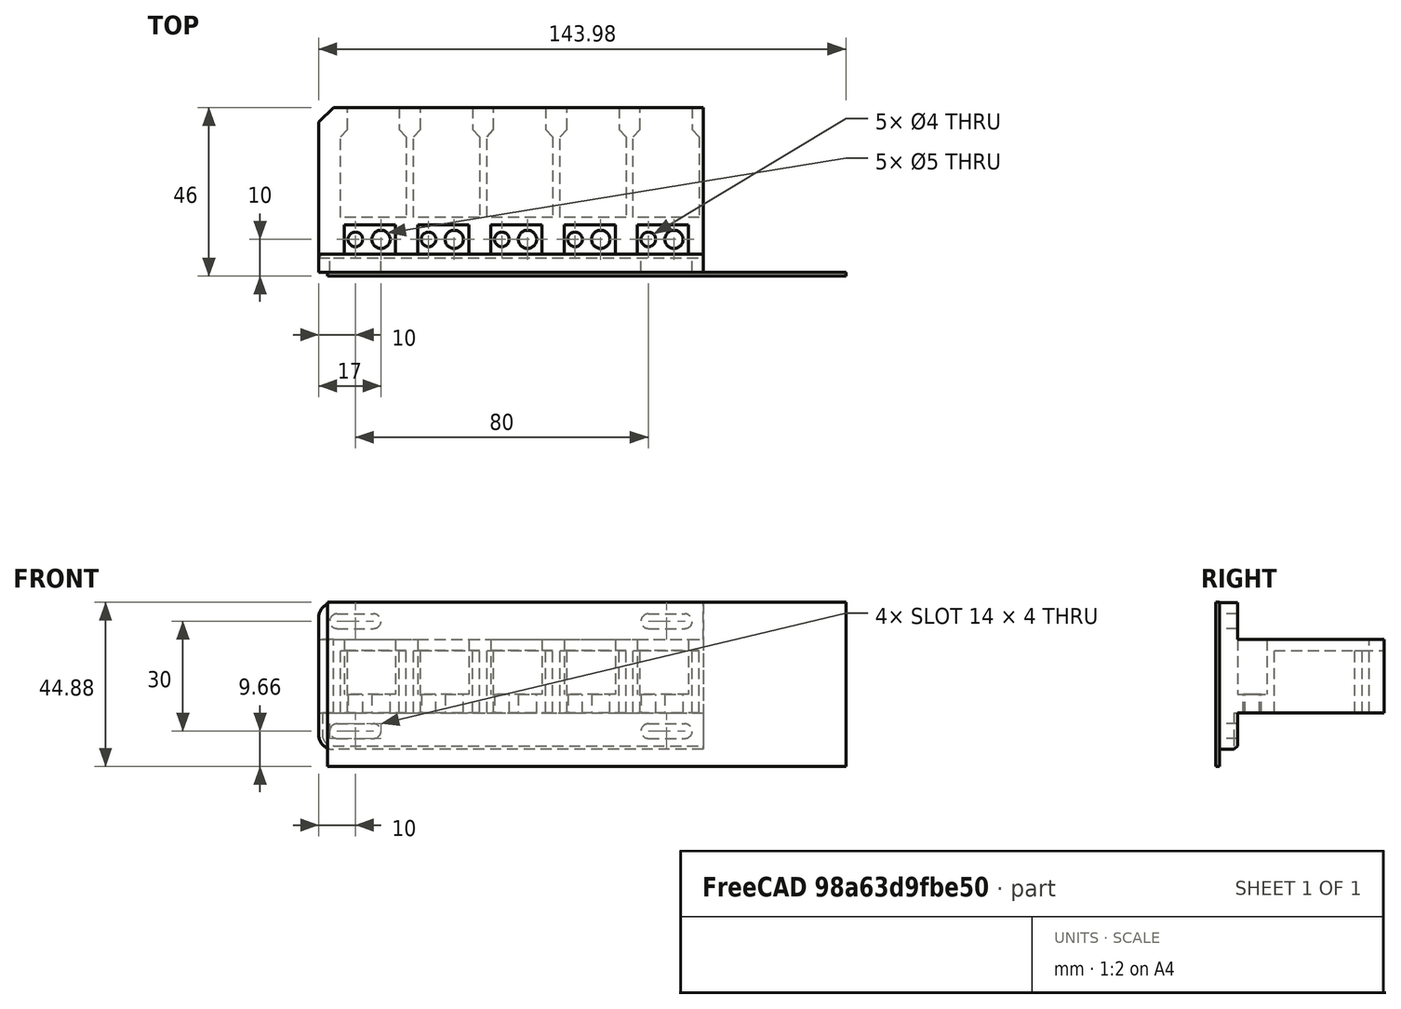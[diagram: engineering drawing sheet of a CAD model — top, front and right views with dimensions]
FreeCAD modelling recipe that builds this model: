
FCSTD DOCUMENT  (FreeCAD 0.18.4R)
Label: switchholder
License: All rights reserved
LicenseURL: http://en.wikipedia.org/wiki/All_rights_reserved
objects: Sketcher::SketchObject×7, Mesh::Feature×5, PartDesign::Pocket×5, PartDesign::LinearPattern×3, PartDesign::Pad×2, PartDesign::Body×2, PartDesign::Chamfer×2, PartDesign::Fillet×1
note: 29 computed .brp shape members not serialized (recipe doc carries the construction recipe); baked Part::Feature solids carry a one-line shape summary decoded from their .brp

FEATURE [Mesh::Feature] v10
  Placement = pos=(0,38,0) rot=(0,0,1;0rad)
FEATURE [Mesh::Feature] v011
  Placement = pos=(20,38,0) rot=(0,0,1;0rad)
FEATURE [Mesh::Feature] v012
  Placement = pos=(-20,38,0) rot=(0,0,1;0rad)
FEATURE [Sketcher::SketchObject] Sketch
  MapMode = 5
  Placement = pos=(0,0,0) rot=(1,0,0;1.5708rad)
  Support = -> [XZ_Plane001]
  sketch-geometry (4):
    g0: LineSegment StartX=-52.6197 StartY=20.2239 StartZ=0 EndX=88.9826 EndY=20.2239 EndZ=0
    g1: LineSegment StartX=88.9826 StartY=20.2239 StartZ=0 EndX=88.9826 EndY=-24.6555 EndZ=0
    g2: LineSegment StartX=88.9826 StartY=-24.6555 StartZ=0 EndX=-52.6197 EndY=-24.6555 EndZ=0
    g3: LineSegment StartX=-52.6197 StartY=-24.6555 StartZ=0 EndX=-52.6197 EndY=20.2239 EndZ=0
  constraints (8):
    c: Coincident(g0,g1)
    c: Coincident(g1,g2)
    c: Coincident(g2,g3)
    c: Coincident(g3,g0)
    c: Horizontal(g0)
    c: Horizontal(g2)
    c: Vertical(g1)
    c: Vertical(g3)
FEATURE [PartDesign::Pad] Pad
  Length = 1
  Length2 = 100
  Placement = pos=(0,0,0) rot=(1,0,0;1.5708rad)
  Profile = -> Sketch
  Refine = true
  Type = 0
FEATURE [PartDesign::Body] Body001
  Group = -> [Sketch,Pad]
  Origin = -> Origin001
  Tip = -> Pad
FEATURE [Mesh::Feature] v013
  Placement = pos=(-40,38,0) rot=(0,0,1;0rad)
FEATURE [Mesh::Feature] v014
  Placement = pos=(40,38,0) rot=(0,0,1;0rad)
FEATURE [Sketcher::SketchObject] Sketch001
  MapMode = 5
  Placement = pos=(0,0,0) rot=(1,0,0;1.5708rad)
  Support = -> [XZ_Plane]
  sketch-geometry (4):
    g0: LineSegment StartX=-55 StartY=20 StartZ=0 EndX=50 EndY=20 EndZ=0
    g1: LineSegment StartX=50 StartY=20 StartZ=0 EndX=50 EndY=-20 EndZ=0
    g2: LineSegment StartX=50 StartY=-20 StartZ=0 EndX=-55 EndY=-20 EndZ=0
    g3: LineSegment StartX=-55 StartY=-20 StartZ=0 EndX=-55 EndY=20 EndZ=0
  constraints (11):
    c: Coincident(g0,g1)
    c: Coincident(g1,g2)
    c: Coincident(g2,g3)
    c: Coincident(g3,g0)
    c: Horizontal(g2)
    c: Vertical(g1)
    c: Vertical(g3)
    c: DistanceX(g0,g0) = 105
    c: DistanceY(g3,g3) = 40
    c: DistanceY(g-1,g0) = 20
    c: DistanceX(g-1,g0) = 50
FEATURE [PartDesign::Pad] Pad001
  Length = 45
  Length2 = 100
  Placement = pos=(0,0,0) rot=(1,0,0;1.5708rad)
  Profile = -> Sketch001
  Refine = true
  Reversed = true
  Type = 0
FEATURE [Sketcher::SketchObject] Sketch002
  ExternalGeometry = -> [Pad001]
  MapMode = 5
  Placement = pos=(-55,0,0) rot=(0.707107,0,-0.707107;3.14159rad)
  Support = -> [Pad001]
  sketch-geometry (8):
    g0: LineSegment StartX=-20 StartY=-45 StartZ=0 EndX=-10 EndY=-45 EndZ=0
    g1: LineSegment StartX=-10 StartY=-45 StartZ=0 EndX=-10 EndY=-5 EndZ=0
    g2: LineSegment StartX=-10 StartY=-5 StartZ=0 EndX=-20 EndY=-5 EndZ=0
    g3: LineSegment StartX=-20 StartY=-5 StartZ=0 EndX=-20 EndY=-45 EndZ=0
    g4: LineSegment StartX=20 StartY=-45 StartZ=0 EndX=10 EndY=-45 EndZ=0
    g5: LineSegment StartX=10 StartY=-45 StartZ=0 EndX=10 EndY=-5 EndZ=0
    g6: LineSegment StartX=10 StartY=-5 StartZ=0 EndX=20 EndY=-5 EndZ=0
    g7: LineSegment StartX=20 StartY=-5 StartZ=0 EndX=20 EndY=-45 EndZ=0
  constraints (22):
    c: Coincident(g0,g1)
    c: Coincident(g1,g2)
    c: Coincident(g2,g3)
    c: Coincident(g3,g0)
    c: Horizontal(g0)
    c: Horizontal(g2)
    c: Vertical(g1)
    c: Vertical(g3)
    c: Coincident(g0,g-3)
    c: Coincident(g4,g5)
    c: Coincident(g5,g6)
    c: Coincident(g6,g7)
    c: Coincident(g7,g4)
    c: Horizontal(g4)
    c: Horizontal(g6)
    c: Vertical(g5)
    c: Vertical(g7)
    c: Coincident(g4,g-4)
    c: Equal(g4,g0)
    c: Horizontal(g1,g5)
    c: DistanceY(g2,g-3) = 5
    c: DistanceX(g2,g2) = 10
FEATURE [PartDesign::Pocket] Pocket
  BaseFeature = -> Pad001
  Length = 5
  Length2 = 100
  Placement = pos=(0,0,0) rot=(1,0,0;1.5708rad)
  Profile = -> Sketch002
  Refine = true
  Type = 1
FEATURE [Sketcher::SketchObject] Sketch003
  ExternalGeometry = -> [Pocket]
  MapMode = 5
  Placement = pos=(0,5,-2.2e-15) rot=(-1,0,0;1.5708rad)
  Support = -> [Pocket]
  sketch-geometry (20):
    g0: ArcOfCircle CenterX=-50 CenterY=15 CenterZ=0 NormalX=0 NormalY=0 NormalZ=1 AngleXU=0 Radius=2 StartAngle=1.5708 EndAngle=4.71239
    g1: ArcOfCircle CenterX=-40 CenterY=15 CenterZ=0 NormalX=0 NormalY=0 NormalZ=1 AngleXU=0 Radius=2 StartAngle=4.71239 EndAngle=7.85398
    g2: LineSegment StartX=-50 StartY=13 StartZ=0 EndX=-40 EndY=13 EndZ=0
    g3: LineSegment StartX=-50 StartY=17 StartZ=0 EndX=-40 EndY=17 EndZ=0
    g4: ArcOfCircle CenterX=35 CenterY=15 CenterZ=0 NormalX=0 NormalY=0 NormalZ=1 AngleXU=0 Radius=2 StartAngle=1.5708 EndAngle=4.71239
    g5: ArcOfCircle CenterX=45 CenterY=15 CenterZ=0 NormalX=0 NormalY=0 NormalZ=1 AngleXU=0 Radius=2 StartAngle=4.71239 EndAngle=7.85398
    g6: LineSegment StartX=35 StartY=13 StartZ=0 EndX=45 EndY=13 EndZ=0
    g7: LineSegment StartX=35 StartY=17 StartZ=0 EndX=45 EndY=17 EndZ=0
    g8: ArcOfCircle CenterX=-50 CenterY=-15 CenterZ=0 NormalX=0 NormalY=0 NormalZ=1 AngleXU=0 Radius=2 StartAngle=1.5708 EndAngle=4.71239
    g9: ArcOfCircle CenterX=-40 CenterY=-15 CenterZ=0 NormalX=0 NormalY=0 NormalZ=1 AngleXU=0 Radius=2 StartAngle=4.71239 EndAngle=7.85398
    g10: LineSegment StartX=-50 StartY=-17 StartZ=0 EndX=-40 EndY=-17 EndZ=0
    g11: LineSegment StartX=-50 StartY=-13 StartZ=0 EndX=-40 EndY=-13 EndZ=0
    g12: ArcOfCircle CenterX=35 CenterY=-15 CenterZ=0 NormalX=0 NormalY=0 NormalZ=1 AngleXU=0 Radius=2 StartAngle=1.5708 EndAngle=4.71239
    g13: ArcOfCircle CenterX=45 CenterY=-15 CenterZ=0 NormalX=0 NormalY=0 NormalZ=1 AngleXU=0 Radius=2 StartAngle=4.71239 EndAngle=7.85398
    g14: LineSegment StartX=35 StartY=-17 StartZ=0 EndX=45 EndY=-17 EndZ=0
    g15: LineSegment StartX=35 StartY=-13 StartZ=0 EndX=45 EndY=-13 EndZ=0
    g16: LineSegment [constr] StartX=-50 StartY=15 StartZ=0 EndX=45 EndY=15 EndZ=0
    g17: LineSegment [constr] StartX=45 StartY=15 StartZ=0 EndX=45 EndY=-15 EndZ=0
    g18: LineSegment [constr] StartX=45 StartY=-15 StartZ=0 EndX=-50 EndY=-15 EndZ=0
    g19: LineSegment [constr] StartX=-50 StartY=-15 StartZ=0 EndX=-50 EndY=15 EndZ=0
  constraints (48):
    c: Tangent(g0,g3) = 1.5708
    c: Tangent(g0,g2) = -1.5708
    c: Tangent(g2,g1) = -1.5708
    c: Tangent(g3,g1) = 1.5708
    c: Horizontal(g2)
    c: Equal(g0,g1)
    c: Tangent(g4,g7) = 1.5708
    c: Tangent(g4,g6) = -1.5708
    c: Tangent(g6,g5) = -1.5708
    c: Tangent(g7,g5) = 1.5708
    c: Horizontal(g6)
    c: Equal(g4,g5)
    c: Tangent(g8,g11) = 1.5708
    c: Tangent(g8,g10) = -1.5708
    c: Tangent(g10,g9) = -1.5708
    c: Tangent(g11,g9) = 1.5708
    c: Horizontal(g10)
    c: Equal(g8,g9)
    c: Tangent(g12,g15) = 1.5708
    c: Tangent(g12,g14) = -1.5708
    c: Tangent(g14,g13) = -1.5708
    c: Tangent(g15,g13) = 1.5708
    c: Horizontal(g14)
    c: Equal(g12,g13)
    c: Equal(g13,g5)
    c: Equal(g5,g1)
    c: Equal(g1,g9)
    c: Radius(g0) = 2
    c: Equal(g3,g11)
    c: Equal(g11,g15)
    c: Equal(g15,g7)
    c: DistanceX(g3,g3) = 10
    c: Coincident(g16,g17)
    c: Coincident(g17,g18)
    c: Coincident(g18,g19)
    c: Coincident(g19,g16)
    c: Horizontal(g18)
    c: Vertical(g17)
    c: Vertical(g19)
    c: Coincident(g16,g0)
    c: Coincident(g17,g13)
    c: Coincident(g5,g16)
    c: Coincident(g8,g18)
    c: DistanceY(g8,g-3) = 5
    c: DistanceY(g-3,g0) = 5
    c: DistanceX(g-3,g0) = 5
    c: DistanceX(g5,g-4) = 5
    c: Horizontal(g16)
FEATURE [PartDesign::Pocket] Pocket001
  BaseFeature = -> Pocket
  Length = 5
  Length2 = 100
  Placement = pos=(0,0,0) rot=(1,0,0;1.5708rad)
  Profile = -> Sketch003
  Refine = true
  Type = 1
FEATURE [Sketcher::SketchObject] Sketch004
  ExternalGeometry = -> [Pocket001]
  MapMode = 5
  Placement = pos=(2.2e-15,-8.9e-15,-10) rot=(1,0,0;3.14159rad)
  Support = -> [Pocket001]
  sketch-geometry (8):
    g0: LineSegment StartX=47 StartY=-45 StartZ=0 EndX=47 EndY=-39 EndZ=0
    g1: LineSegment StartX=47 StartY=-39 StartZ=0 EndX=48.9 EndY=-37 EndZ=0
    g2: LineSegment StartX=48.9 StartY=-37 StartZ=0 EndX=48.9 EndY=-15 EndZ=0
    g3: LineSegment StartX=48.9 StartY=-15 StartZ=0 EndX=30.9 EndY=-15 EndZ=0
    g4: LineSegment StartX=30.9 StartY=-15 StartZ=0 EndX=30.9 EndY=-37 EndZ=0
    g5: LineSegment StartX=30.9 StartY=-37 StartZ=0 EndX=32.8 EndY=-39 EndZ=0
    g6: LineSegment StartX=32.8 StartY=-39 StartZ=0 EndX=32.8 EndY=-45 EndZ=0
    g7: LineSegment StartX=32.8 StartY=-45 StartZ=0 EndX=47 EndY=-45 EndZ=0
  constraints (24):
    c: Coincident(g0,g1)
    c: Coincident(g1,g2)
    c: Vertical(g2)
    c: Coincident(g2,g3)
    c: Horizontal(g3)
    c: Coincident(g3,g4)
    c: Vertical(g4)
    c: Coincident(g4,g5)
    c: Coincident(g5,g6)
    c: PointOnObject(g6,g-3)
    c: Coincident(g6,g7)
    c: Coincident(g7,g0)
    c: Horizontal(g7)
    c: Vertical(g6)
    c: Equal(g5,g1)
    c: Vertical(g0)
    c: Horizontal(g0,g5)
    c: Equal(g4,g2)
    c: DistanceX(g7,g7) = 14.2
    c: DistanceX(g3,g3) = 18
    c: DistanceY(g1,g1) = 2
    c: DistanceY(g0,g0) = 6
    c: DistanceY(g6,g3) = 30
    c: DistanceX(g0,g-3) = 3
FEATURE [PartDesign::Pocket] Pocket002
  BaseFeature = -> Pocket001
  Length = 17
  Length2 = 100
  Placement = pos=(0,0,0) rot=(1,0,0;1.5708rad)
  Profile = -> Sketch004
  Refine = true
  Type = 0
FEATURE [PartDesign::LinearPattern] LinearPattern
  BaseFeature = -> Pocket002
  Direction = -> Sketch004 [H_Axis]
  Length = 80
  Occurrences = 5
  Originals = -> [Pocket002]
  Placement = pos=(0,0,0) rot=(1,0,0;1.5708rad)
  Refine = true
  Reversed = true
FEATURE [Sketcher::SketchObject] Sketch005
  ExternalGeometry = -> [LinearPattern]
  MapMode = 5
  Placement = pos=(-2.2e-15,1.33e-14,10) rot=(0,0,1;3.14159rad)
  Support = -> [LinearPattern]
  sketch-geometry (4):
    g0: LineSegment StartX=-46 StartY=-5 StartZ=0 EndX=-32 EndY=-5 EndZ=0
    g1: LineSegment StartX=-32 StartY=-5 StartZ=0 EndX=-32 EndY=-13 EndZ=0
    g2: LineSegment StartX=-32 StartY=-13 StartZ=0 EndX=-46 EndY=-13 EndZ=0
    g3: LineSegment StartX=-46 StartY=-13 StartZ=0 EndX=-46 EndY=-5 EndZ=0
  constraints (12):
    c: Coincident(g0,g1)
    c: Coincident(g1,g2)
    c: Coincident(g2,g3)
    c: Coincident(g3,g0)
    c: Horizontal(g0)
    c: Horizontal(g2)
    c: Vertical(g1)
    c: Vertical(g3)
    c: DistanceX(g-3,g0) = 4
    c: PointOnObject(g0,g-3)
    c: DistanceX(g2,g2) = 14
    c: DistanceY(g1,g1) = 8
FEATURE [PartDesign::Pocket] Pocket003
  BaseFeature = -> LinearPattern
  Length = 15
  Length2 = 100
  Placement = pos=(0,0,0) rot=(1,0,0;1.5708rad)
  Profile = -> Sketch005
  Refine = true
  Type = 0
FEATURE [PartDesign::LinearPattern] LinearPattern001
  BaseFeature = -> Pocket003
  Direction = -> Sketch005 [H_Axis]
  Length = 80
  Occurrences = 5
  Originals = -> [Pocket003]
  Placement = pos=(0,0,0) rot=(1,0,0;1.5708rad)
  Refine = true
FEATURE [Sketcher::SketchObject] Sketch006
  ExternalGeometry = -> [LinearPattern001]
  MapMode = 5
  Placement = pos=(1.3e-15,-8.9e-15,-5) rot=(0,0,1;3.14159rad)
  Support = -> [LinearPattern001]
  sketch-geometry (3):
    g0: Circle CenterX=-42 CenterY=-9 CenterZ=0 NormalX=0 NormalY=0 NormalZ=1 AngleXU=0 Radius=2.5
    g1: Circle CenterX=-35 CenterY=-9 CenterZ=0 NormalX=0 NormalY=0 NormalZ=1 AngleXU=0 Radius=2
    g2: LineSegment [constr] StartX=-46 StartY=-9 StartZ=0 EndX=-32 EndY=-9 EndZ=0
  constraints (9):
    c: Radius(g0) = 2.5
    c: PointOnObject(g2,g-4)
    c: Horizontal(g2)
    c: Symmetric(g-3,g-3,g2)
    c: PointOnObject(g0,g2)
    c: Radius(g1) = 2
    c: DistanceX(g-3,g0) = 4
    c: PointOnObject(g1,g2)
    c: DistanceX(g1,g-4) = 3
FEATURE [PartDesign::Pocket] Pocket004
  BaseFeature = -> LinearPattern001
  Length = 5
  Length2 = 100
  Placement = pos=(0,0,0) rot=(1,0,0;1.5708rad)
  Profile = -> Sketch006
  Refine = true
  Type = 1
FEATURE [PartDesign::LinearPattern] LinearPattern002
  BaseFeature = -> Pocket004
  Direction = -> Sketch006 [H_Axis]
  Length = 80
  Occurrences = 5
  Originals = -> [Pocket004]
  Placement = pos=(0,0,0) rot=(1,0,0;1.5708rad)
  Refine = true
FEATURE [PartDesign::Fillet] Fillet
  Base = -> LinearPattern002 [Edge64,Edge4]
  BaseFeature = -> LinearPattern002
  Placement = pos=(0,0,0) rot=(1,0,0;1.5708rad)
  Radius = 4
FEATURE [PartDesign::Chamfer] Chamfer
  Base = -> Fillet [Edge70]
  BaseFeature = -> Fillet
  Placement = pos=(0,0,0) rot=(1,0,0;1.5708rad)
  Size = 1
FEATURE [PartDesign::Chamfer] Chamfer001
  Base = -> Chamfer [Edge149]
  BaseFeature = -> Chamfer
  Placement = pos=(0,0,0) rot=(1,0,0;1.5708rad)
  Size = 4
FEATURE [PartDesign::Body] Body
  Group = -> [Sketch001,Pad001,Sketch002,Pocket,Sketch003,Pocket001,Sketch004,Pocket002,LinearPattern,Sketch005,Pocket003,LinearPattern001,Sketch006,Pocket004,LinearPattern002,Fillet,Chamfer,Chamfer001]
  Origin = -> Origin
  Tip = -> Chamfer001
